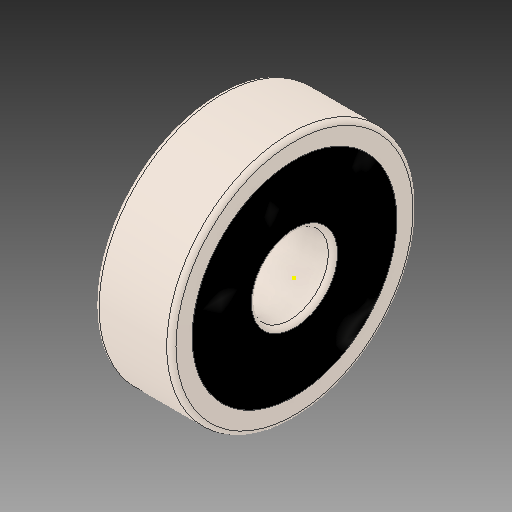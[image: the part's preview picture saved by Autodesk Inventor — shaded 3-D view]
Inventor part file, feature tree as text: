
AUTODESK INVENTOR PART (.ipt)
format: ipt  version: 2017 (Build 210142000, 142)  size: 2,316,288 bytes
history: imported  units: mm
features: other x22, sketch x3, imported_body x1
ambient origin geometry x8: Origin, YZ Plane, XZ Plane, XY Plane, X Axis, Y Axis, Z Axis, Center Point
bodies: Solid1 (imported_parasolid), Solid2 (imported_parasolid), Solid3 (imported_parasolid), Solid4 (imported_parasolid), Solid5 (imported_parasolid), Solid6 (imported_parasolid), Solid7 (imported_parasolid), Solid8 (imported_parasolid), Solid9 (imported_parasolid), Solid10 (imported_parasolid), Solid11 (imported_parasolid), Solid12 (imported_parasolid), Solid13 (imported_parasolid), Solid14 (imported_parasolid), Solid15 (imported_parasolid), Solid16 (imported_parasolid), Solid17 (imported_parasolid), Solid18 (imported_parasolid), Solid19 (imported_parasolid), Solid20 (imported_parasolid)
feature tree (26):
  other  "SKF 625_MIR1.ipt"
  other  "Solid1::SKF 625_MIR1.ipt"
  other  "Solid2::SKF 625_MIR1.ipt"
  other  "Solid3::SKF 625_MIR1.ipt"
  other  "Solid4::SKF 625_MIR1.ipt"
  other  "Solid5::SKF 625_MIR1.ipt"
  other  "Solid6::SKF 625_MIR1.ipt"
  other  "Solid7::SKF 625_MIR1.ipt"
  other  "Solid8::SKF 625_MIR1.ipt"
  other  "Solid9::SKF 625_MIR1.ipt"
  other  "Solid10::SKF 625_MIR1.ipt"
  other  "Solid11::SKF 625_MIR1.ipt"
  other  "Solid12::SKF 625_MIR1.ipt"
  other  "Solid13::SKF 625_MIR1.ipt"
  other  "Solid14::SKF 625_MIR1.ipt"
  other  "Solid15::SKF 625_MIR1.ipt"
  other  "Solid16::SKF 625_MIR1.ipt"
  other  "Solid17::SKF 625_MIR1.ipt"
  other  "Solid18::SKF 625_MIR1.ipt"
  other  "Solid19::SKF 625_MIR1.ipt"
  other  "Solid20::SKF 625_MIR1.ipt"
  other  "TaggingFeature1"
  sketch  "Sketch1"  dims[d0=10.0mm]
  sketch  "Sketch2"
  sketch  "Sketch3"
  imported_body  NMx_Import_Brep_tag  [imported B-rep: ~49 faces, bbox_mm=None]
